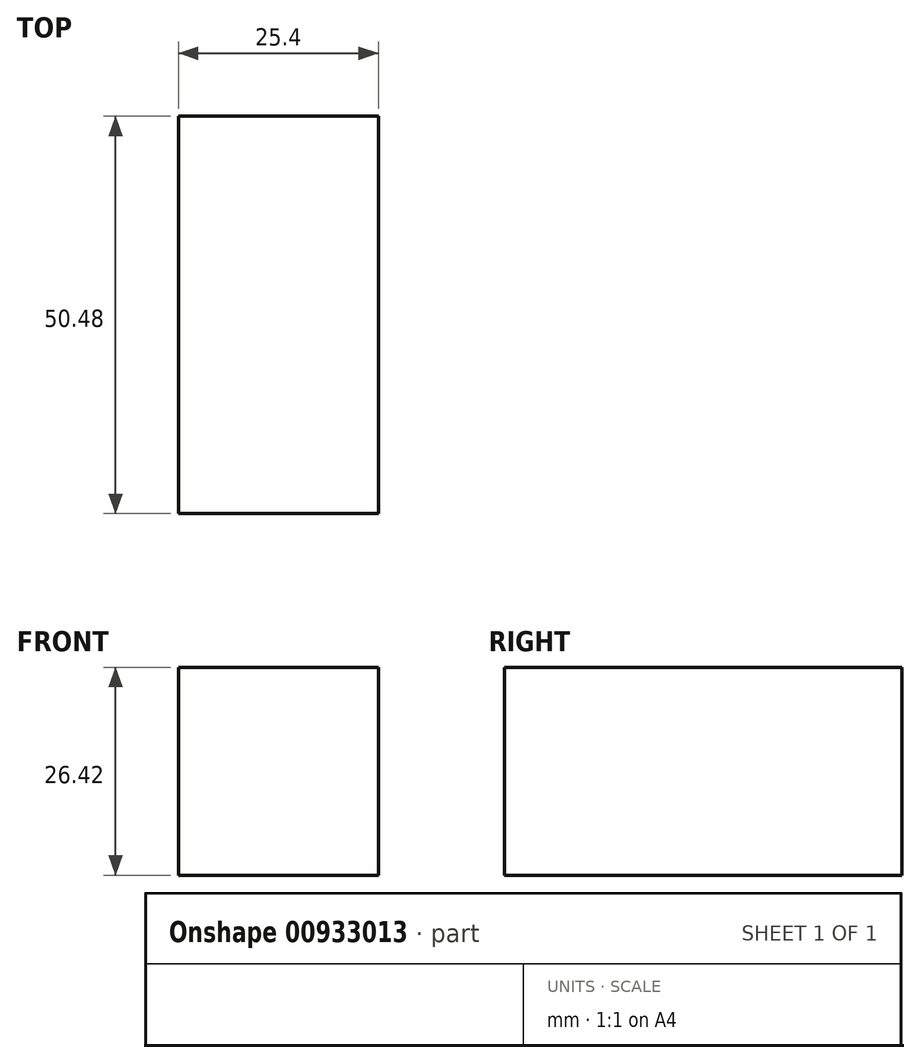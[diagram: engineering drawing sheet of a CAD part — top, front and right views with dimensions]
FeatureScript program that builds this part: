
annotation { "Feature Type Name" : "Feature", "Feature Type Description" : "" }
export const myFeature = defineFeature(function(context is Context, id is Id, definition is map)
    precondition{}
    {
        {
            var Q0;
            Q0=qCreatedBy(makeId("Front.planeOp"),FACE);
            var sketch = newSketch(context, id + "F0", { "sketchPlane" : qUnion([Q0])});
            skLineSegment(sketch, "E0", {"start": v(-20.37, -28.67) * mm, "end": v(0, -28.67) * mm});
            skLineSegment(sketch, "E1", {"start": v(0, -28.67) * mm, "end": v(0, 22.65) * mm});
            skLineSegment(sketch, "E2", {"start": v(0, 22.65) * mm, "end": v(-20.37, 22.65) * mm});
            skLineSegment(sketch, "E3", {"start": v(-20.37, 22.65) * mm, "end": v(-38.63, 8.43) * mm});
            skLineSegment(sketch, "E4", {"start": v(-38.63, 8.43) * mm, "end": v(-38.63, -9.97) * mm});
            skLineSegment(sketch, "E5", {"start": v(-38.63, -9.97) * mm, "end": v(-20.37, -28.67) * mm});
            skSolve(sketch);
        }
        {
            var Q0;
            Q0=makeQuery(id+"F0.imprint","IMPRINT",FACE,{"disambiguationData":[TD([[makeQuery(id+"F0.imprint","IMPRINT",EDGE,{"derivedFrom":sQuery(id+"F0.wireOp",EDGE,"E0")}),1.0]])]});
            var Q1;
            Q1 = qSketchRegion(id + "F0", true);
            extrude(context, id + "F1", {"entities" : qUnion([Q0, Q1]), "oppositeDirection" : true, "depth" : 127 * mm, "offsetDistance" : 25.4 * mm});
        }
        {
            var Q0;
            Q0=makeQuery(id+"F1.opExtrude","SWEPT_BODY",BODY,{"disambiguationData":[OSD([sQuery(id+"F0.wireOp",EDGE,"E0"),sQuery(id+"F0.wireOp",EDGE,"E1"),sQuery(id+"F0.wireOp",EDGE,"E2"),sQuery(id+"F0.wireOp",EDGE,"E3"),sQuery(id+"F0.wireOp",EDGE,"E4"),sQuery(id+"F0.wireOp",EDGE,"E5")])]});
            deleteBodies(context, id + "F2", {"entities" : qUnion([Q0])});
        }
        {
            var Q0;
            Q0=qCreatedBy(makeId("Right.planeOp"),FACE);
            var sketch = newSketch(context, id + "F3", { "sketchPlane" : qUnion([Q0])});
            skLineSegment(sketch, "E6.bottom", {"start": v(0, 15.95) * mm, "end": v(50.48, 15.95) * mm});
            skLineSegment(sketch, "E6.top", {"start": v(0, -10.47) * mm, "end": v(50.48, -10.47) * mm});
            skLineSegment(sketch, "E6.left", {"start": v(0, 15.95) * mm, "end": v(0, -10.47) * mm});
            skLineSegment(sketch, "E6.right", {"start": v(50.48, 15.95) * mm, "end": v(50.48, -10.47) * mm});
            skCircle(sketch, "E7", {"center": v(16.23, 7.02) * mm, "radius": 4.09 * mm});
            skSolve(sketch);
        }
        {
            var Q0;
            Q0 = qSketchRegion(id + "F3", true);
            var Q1;
            Q1=makeQuery(id+"F3.imprint","IMPRINT",FACE,{"disambiguationData":[TD([[makeQuery(id+"F3.imprint","IMPRINT",EDGE,{"derivedFrom":sQuery(id+"F3.wireOp",EDGE,"E7")}),1.0]])]});
            extrude(context, id + "F4", {"entities" : qUnion([Q0, Q1]), "depth" : 25.4 * mm, "offsetDistance" : 25.4 * mm});
        }
    });
